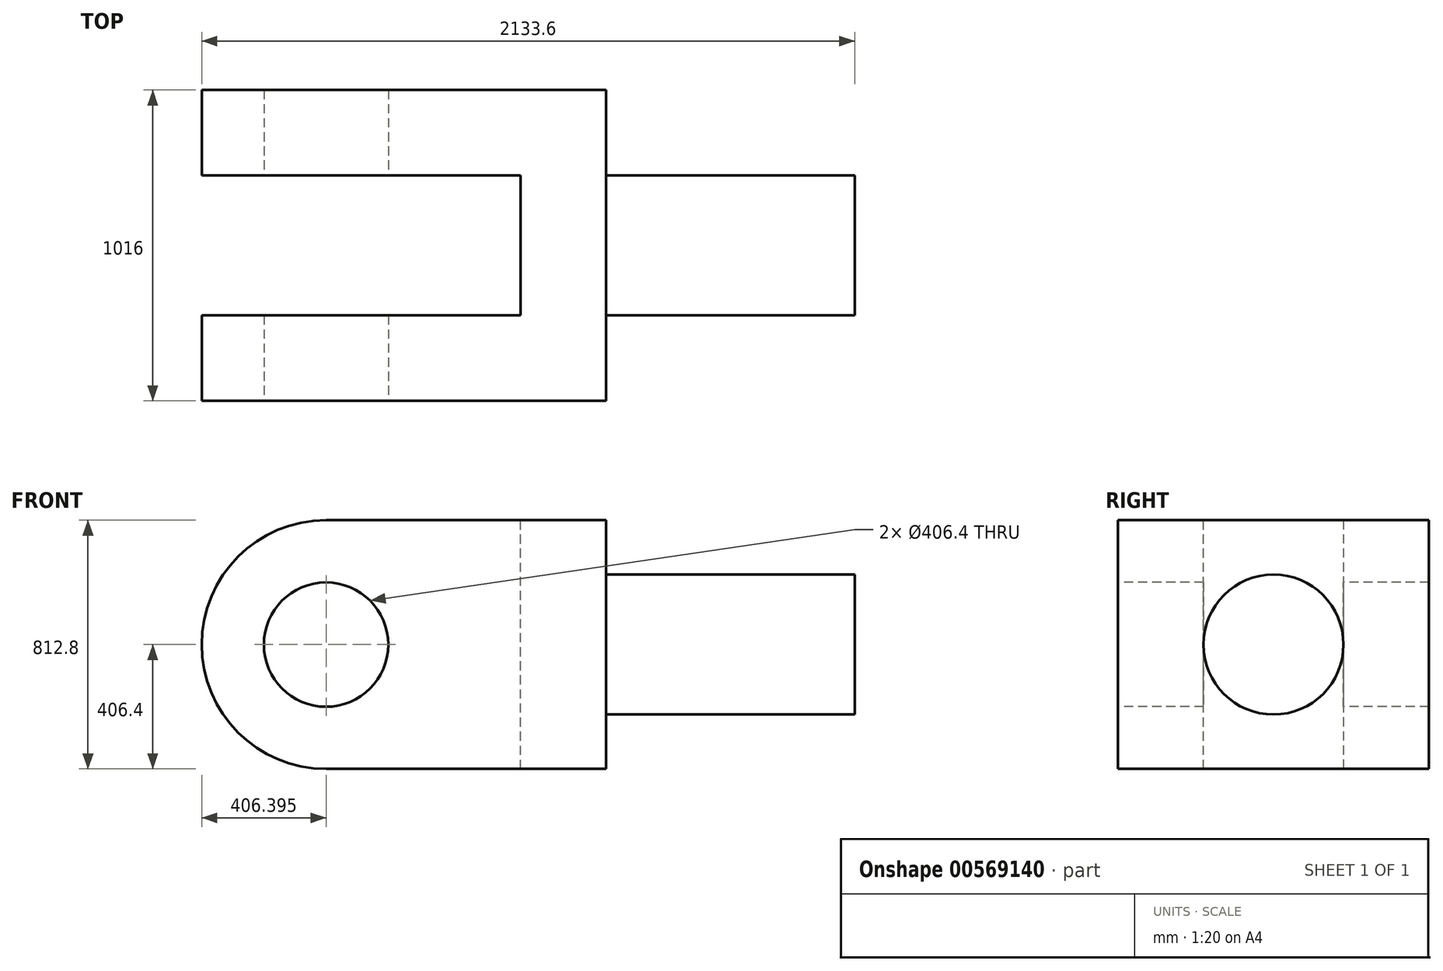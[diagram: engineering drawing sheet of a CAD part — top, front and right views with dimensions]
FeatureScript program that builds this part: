
annotation { "Feature Type Name" : "Feature", "Feature Type Description" : "" }
export const myFeature = defineFeature(function(context is Context, id is Id, definition is map)
    precondition{}
    {
        {
            var Q0;
            Q0=qCreatedBy(makeId("Top.planeOp"),FACE);
            var sketch = newSketch(context, id + "F0", { "sketchPlane" : qUnion([Q0])});
            skLineSegment(sketch, "E0", {"start": v(-128.41, 315.3) * mm, "end": v(-128.41, 35.9) * mm});
            skLineSegment(sketch, "E1", {"start": v(-128.41, 35.9) * mm, "end": v(912.99, 35.9) * mm});
            skLineSegment(sketch, "E2", {"start": v(912.99, 35.9) * mm, "end": v(912.99, -421.3) * mm});
            skLineSegment(sketch, "E3", {"start": v(912.99, -421.3) * mm, "end": v(-128.41, -421.3) * mm});
            skLineSegment(sketch, "E4", {"start": v(-128.41, -421.3) * mm, "end": v(-128.41, -700.7) * mm});
            skLineSegment(sketch, "E5", {"start": v(-128.41, -700.7) * mm, "end": v(1192.39, -700.7) * mm});
            skLineSegment(sketch, "E6", {"start": v(1192.39, -700.7) * mm, "end": v(1192.39, -421.3) * mm});
            skLineSegment(sketch, "E7", {"start": v(1192.39, -421.3) * mm, "end": v(2005.19, -421.3) * mm});
            skLineSegment(sketch, "E8", {"start": v(2005.19, -421.3) * mm, "end": v(2005.19, 35.9) * mm});
            skLineSegment(sketch, "E9", {"start": v(2005.19, 35.9) * mm, "end": v(1192.39, 35.9) * mm});
            skLineSegment(sketch, "E10", {"start": v(1192.39, 35.9) * mm, "end": v(1192.39, 315.3) * mm});
            skLineSegment(sketch, "E11", {"start": v(1192.39, 315.3) * mm, "end": v(-128.41, 315.3) * mm});
            skSolve(sketch);
        }
        {
            var Q0;
            Q0=makeQuery(id+"F0.imprint","IMPRINT",FACE,{"disambiguationData":[TD([[makeQuery(id+"F0.imprint","IMPRINT",EDGE,{"derivedFrom":sQuery(id+"F0.wireOp",EDGE,"E0")}),1.0]])]});
            extrude(context, id + "F1", {"entities" : qUnion([Q0]), "oppositeDirection" : true, "depth" : 812.8 * mm, "offsetDistance" : 25.4 * mm});
        }
        {
            var Q0;
            Q0=makeQuery(id+"F1.opExtrude","SWEPT_FACE",FACE,{"disambiguationData":[OSD([sQuery(id+"F0.wireOp",EDGE,"E7")])]});
            var sketch = newSketch(context, id + "F2", { "sketchPlane" : qUnion([Q0])});
            skLineSegment(sketch, "E12", {"start": v(1192.39, -177.8) * mm, "end": v(2005.19, -177.8) * mm});
            skLineSegment(sketch, "E13", {"start": v(2005.19, -635) * mm, "end": v(1192.39, -635) * mm});
            skSolve(sketch);
        }
        {
            var Q0;
            {var subQ0=sQuery(id+"F2.wireOp",EDGE,"E12");Q0=makeQuery(id+"F2.imprint","IMPRINT",FACE,{"disambiguationData":[TD([[makeQuery(id+"F2.imprint","IMPRINT",EDGE,{"derivedFrom":subQ0}),1.0]])]});}
            var Q1;
            {var subQ0=sQuery(id+"F2.wireOp",EDGE,"E13");Q1=makeQuery(id+"F2.imprint","IMPRINT",FACE,{"disambiguationData":[TD([[makeQuery(id+"F2.imprint","IMPRINT",EDGE,{"derivedFrom":subQ0}),1.0]])]});}
            extrude(context, id + "F3", {"entities" : qUnion([Q0, Q1]), "operationType" : NewBodyOperationType.REMOVE, "endBound" : BoundingType.THROUGH_ALL, "oppositeDirection" : true, "depth" : 25.4 * mm, "offsetDistance" : 25.4 * mm});
        }
        {
            var Q0;
            Q0=makeQuery(id+"F1.opExtrude","SWEPT_FACE",FACE,{"disambiguationData":[OSD([sQuery(id+"F0.wireOp",EDGE,"E5")])]});
            var sketch = newSketch(context, id + "F4", { "sketchPlane" : qUnion([Q0])});
            skArc(sketch, "E14", {"start": v(277.99, 0) * mm, "mid": v(-128.41, -406.4) * mm, "end": v(277.99, -812.8) * mm});
            skPoint(sketch, "E14.first.point", {"position": v(-128.41, -406.4) * mm});
            skPoint(sketch, "E14.second.point", {"position": v(277.99, -812.8) * mm});
            skPoint(sketch, "E14.third.point", {"position": v(277.99, 0) * mm});
            skCircle(sketch, "E15", {"center": v(277.99, -406.4) * mm, "radius": 203.2 * mm});
            skSolve(sketch);
        }
        {
            var Q0;
            {var subQ0=sQuery(id+"F4.wireOp",EDGE,"E14");var subQ1=sQuery(id+"F0.wireOp",EDGE,"E5");var subQ2=makeQuery(id+"F1.opExtrude","CAP_EDGE",EDGE,{"disambiguationData":[OSD([subQ1])],"isStart":true});var subQ3=makeQuery(id+"F4.imprint","INTERSECT",VERTEX,{"derivedFrom":[subQ2,subQ0]});Q0=makeQuery(id+"F4.imprint","IMPRINT",FACE,{"disambiguationData":[TD([[makeQuery(id+"F4.imprint","IMPRINT",EDGE,{"disambiguationData":[TD([[subQ3,-1.0]])],"derivedFrom":subQ0}),-1.0]])]});}
            var Q1;
            {var subQ0=sQuery(id+"F4.wireOp",EDGE,"E14");var subQ1=sQuery(id+"F0.wireOp",EDGE,"E5");var subQ2=makeQuery(id+"F1.opExtrude","CAP_EDGE",EDGE,{"disambiguationData":[OSD([subQ1])],"isStart":false});var subQ3=makeQuery(id+"F4.imprint","INTERSECT",VERTEX,{"derivedFrom":[subQ2,subQ0]});Q1=makeQuery(id+"F4.imprint","IMPRINT",FACE,{"disambiguationData":[TD([[makeQuery(id+"F4.imprint","IMPRINT",EDGE,{"disambiguationData":[TD([[subQ3,1.0]])],"derivedFrom":subQ0}),-1.0]])]});}
            var Q2;
            Q2=makeQuery(id+"F4.imprint","IMPRINT",FACE,{"disambiguationData":[TD([[makeQuery(id+"F4.imprint","IMPRINT",EDGE,{"derivedFrom":sQuery(id+"F4.wireOp",EDGE,"E15")}),1.0]])]});
            extrude(context, id + "F5", {"entities" : qUnion([Q0, Q1, Q2]), "operationType" : NewBodyOperationType.REMOVE, "endBound" : BoundingType.THROUGH_ALL, "oppositeDirection" : true, "depth" : 25.4 * mm, "offsetDistance" : 25.4 * mm});
        }
        {
            var Q0;
            Q0=makeQuery(id+"F1.opExtrude","SWEPT_FACE",FACE,{"disambiguationData":[OSD([sQuery(id+"F0.wireOp",EDGE,"E8")])]});
            var sketch = newSketch(context, id + "F6", { "sketchPlane" : qUnion([Q0])});
            skCircle(sketch, "E16", {"center": v(-192.7, -406.4) * mm, "radius": 228.6 * mm});
            skPoint(sketch, "E16.centerSnap0", {"position": v(35.9, -406.4) * mm});
            skPoint(sketch, "E16.centerSnap1", {"position": v(-192.7, -177.8) * mm});
            skSolve(sketch);
        }
        {
            var Q0;
            {var subQ0=sQuery(id+"F6.wireOp",EDGE,"E16");var subQ1=sQuery(id+"F0.wireOp",EDGE,"E8");var subQ2=sQuery(id+"F0.wireOp",EDGE,"E7");var subQ5=makeQuery(id+"F1.opExtrude","SWEPT_EDGE",EDGE,{"disambiguationData":[OSD([subQ2,subQ1])]});var subQ6=makeQuery(id+"F6.imprint","INTERSECT",VERTEX,{"derivedFrom":[subQ5,subQ0]});Q0=makeQuery(id+"F6.imprint","IMPRINT",FACE,{"disambiguationData":[TD([[makeQuery(id+"F6.imprint","IMPRINT",EDGE,{"disambiguationData":[TD([[subQ6,1.0]])],"derivedFrom":subQ0}),-1.0]])]});}
            var Q1;
            {var subQ0=sQuery(id+"F6.wireOp",EDGE,"E16");var subQ1=sQuery(id+"F0.wireOp",EDGE,"E8");var subQ4=makeQuery(id+"F1.opExtrude","SWEPT_EDGE",EDGE,{"disambiguationData":[OSD([subQ1,sQuery(id+"F0.wireOp",EDGE,"E9")])]});var subQ5=makeQuery(id+"F6.imprint","INTERSECT",VERTEX,{"derivedFrom":[subQ4,subQ0]});Q1=makeQuery(id+"F6.imprint","IMPRINT",FACE,{"disambiguationData":[TD([[makeQuery(id+"F6.imprint","IMPRINT",EDGE,{"disambiguationData":[TD([[subQ5,-1.0]])],"derivedFrom":subQ0}),-1.0]])]});}
            var Q2;
            {var subQ0=sQuery(id+"F6.wireOp",EDGE,"E16");var subQ1=sQuery(id+"F0.wireOp",EDGE,"E8");var subQ2=sQuery(id+"F0.wireOp",EDGE,"E7");var subQ3=makeQuery(id+"F1.opExtrude","SWEPT_EDGE",EDGE,{"disambiguationData":[OSD([subQ2,subQ1])]});var subQ4=makeQuery(id+"F6.imprint","INTERSECT",VERTEX,{"derivedFrom":[subQ3,subQ0]});Q2=makeQuery(id+"F6.imprint","IMPRINT",FACE,{"disambiguationData":[TD([[makeQuery(id+"F6.imprint","IMPRINT",EDGE,{"disambiguationData":[TD([[subQ4,-1.0]])],"derivedFrom":subQ0}),-1.0]])]});}
            var Q3;
            {var subQ0=sQuery(id+"F6.wireOp",EDGE,"E16");var subQ1=sQuery(id+"F0.wireOp",EDGE,"E8");var subQ2=makeQuery(id+"F1.opExtrude","SWEPT_EDGE",EDGE,{"disambiguationData":[OSD([subQ1,sQuery(id+"F0.wireOp",EDGE,"E9")])]});var subQ3=makeQuery(id+"F6.imprint","INTERSECT",VERTEX,{"derivedFrom":[subQ2,subQ0]});Q3=makeQuery(id+"F6.imprint","IMPRINT",FACE,{"disambiguationData":[TD([[makeQuery(id+"F6.imprint","IMPRINT",EDGE,{"disambiguationData":[TD([[subQ3,1.0]])],"derivedFrom":subQ0}),-1.0]])]});}
            extrude(context, id + "F7", {"entities" : qUnion([Q0, Q1, Q2, Q3]), "operationType" : NewBodyOperationType.REMOVE, "oppositeDirection" : true, "depth" : 812.8 * mm, "offsetDistance" : 25.4 * mm});
        }
    });
